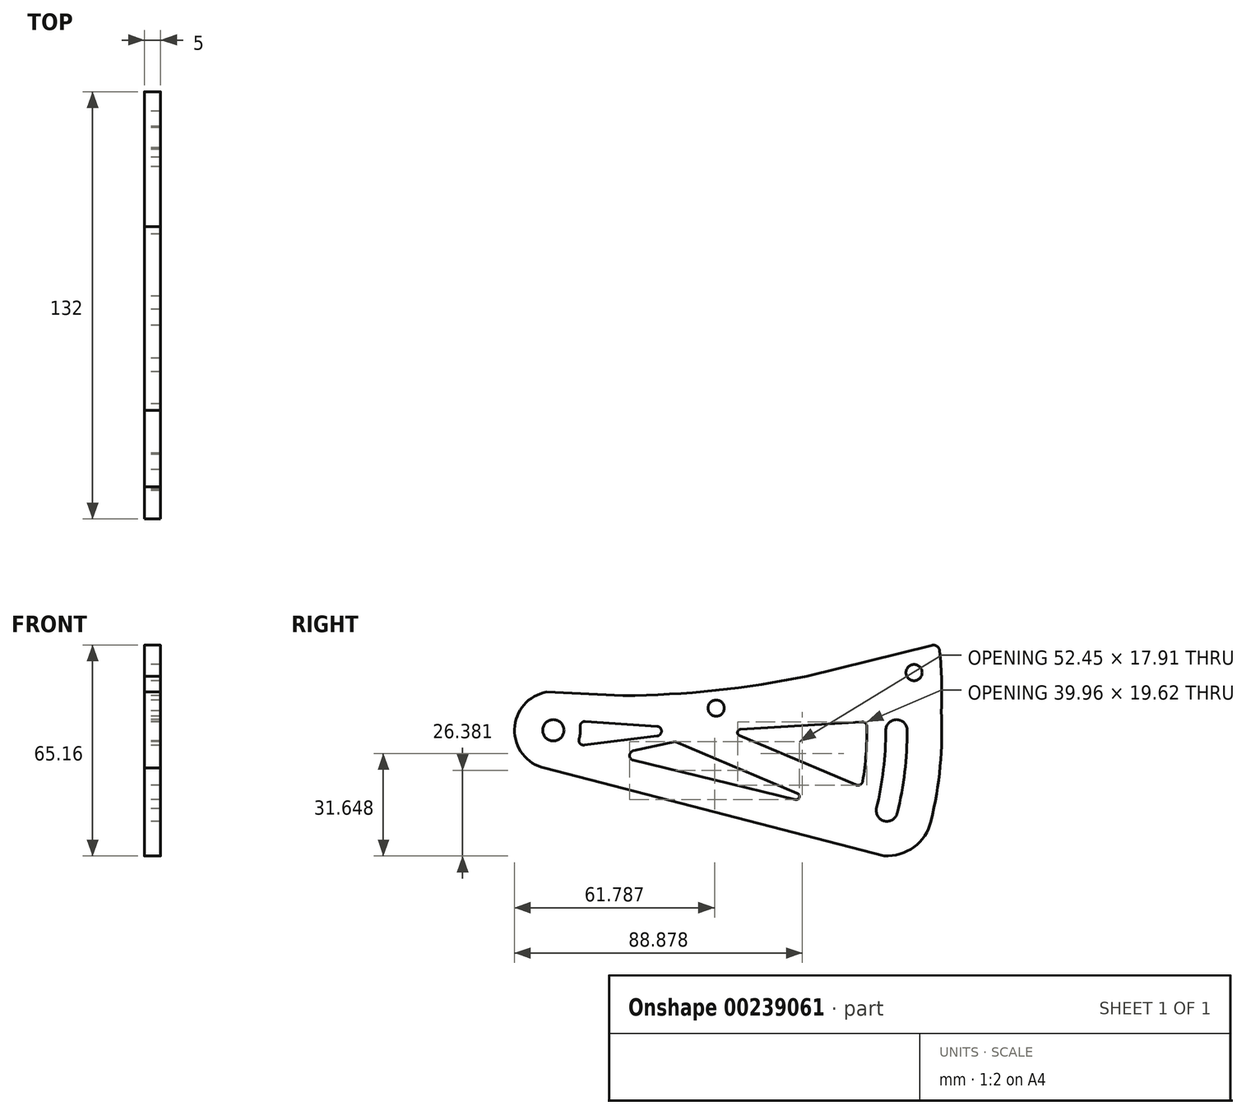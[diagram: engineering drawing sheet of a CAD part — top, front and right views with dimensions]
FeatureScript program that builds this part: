
annotation { "Feature Type Name" : "Feature", "Feature Type Description" : "" }
export const myFeature = defineFeature(function(context is Context, id is Id, definition is map)
    precondition{}
    {
        {
            var Q0;
            Q0=qCreatedBy(makeId("Right.planeOp"),FACE);
            var sketch = newSketch(context, id + "F0", { "sketchPlane" : qUnion([Q0])});
            skLineSegment(sketch, "E0", {"start": v(0, 0) * mm, "end": v(3.3, 0) * mm});
            skArc(sketch, "E1", {"start": v(98.88, -38.19) * mm, "mid": v(98.92, -38.08) * mm, "end": v(98.97, -37.97) * mm});
            skArc(sketch, "E2", {"start": v(109.3, 0) * mm, "mid": v(106, 3.3) * mm, "end": v(102.7, 0) * mm});
            skArc(sketch, "E3", {"start": v(95.75, -37.14) * mm, "mid": v(95.8, -36.99) * mm, "end": v(95.87, -36.84) * mm});
            skArc(sketch, "E4", {"start": v(106.26, -25.6) * mm, "mid": v(108.54, -12.89) * mm, "end": v(109.3, 0) * mm});
            skArc(sketch, "E5", {"start": v(116.66, -28.1) * mm, "mid": v(119.48, -11.17) * mm, "end": v(119.85, 6) * mm});
            skArc(sketch, "E6", {"start": v(99.84, -24.05) * mm, "mid": v(102.58, -28.1) * mm, "end": v(106.35, -25) * mm});
            skArc(sketch, "E7", {"start": v(0, 12) * mm, "mid": v(-11.92, 1.35) * mm, "end": v(-2.68, -11.7) * mm});
            skLineSegment(sketch, "E8", {"start": v(-3.32, -11.53) * mm, "end": v(102.18, -38.8) * mm});
            skArc(sketch, "E9.trimOffspring", {"start": v(106.35, -25) * mm, "mid": v(106.38, -25) * mm, "end": v(106.4, -25) * mm});
            skArc(sketch, "E10.trimOffspring", {"start": v(99.8, -24.22) * mm, "mid": v(101.97, -12.2) * mm, "end": v(102.7, 0) * mm});
            skArc(sketch, "E11.trimOffspring", {"start": v(99.8, -24.22) * mm, "mid": v(99.8, -24.22) * mm, "end": v(99.8, -24.22) * mm});
            skArc(sketch, "E12.trimOffspring", {"start": v(102.18, -38.8) * mm, "mid": v(111.37, -36.09) * mm, "end": v(116.66, -28.1) * mm});
            skArc(sketch, "E13", {"start": v(21.96, 10.72) * mm, "mid": v(21.96, 10.73) * mm, "end": v(21.96, 10.73) * mm});
            skArc(sketch, "E14", {"start": v(119.85, 6) * mm, "mid": v(119.96, 15.28) * mm, "end": v(119.34, 24.54) * mm});
            skArc(sketch, "E15", {"start": v(21.46, 10.73) * mm, "mid": v(22.07, 10.72) * mm, "end": v(22.67, 10.8) * mm});
            skLineSegment(sketch, "E16", {"start": v(21.83, 10.72) * mm, "end": v(-2.06, 11.82) * mm});
            skLineSegment(sketch, "E17", {"start": v(78.34, 16.72) * mm, "end": v(116.87, 26.27) * mm});
            skCircle(sketch, "E18", {"center": v(0, 0) * mm, "radius": 3.3 * mm});
            skPoint(sketch, "E19.orphan", {"position": v(21.83, 9.28) * mm});
            skPoint(sketch, "E20.third.point", {"position": v(50.09, 12.3) * mm});
            skPoint(sketch, "E20.third.point.positionSnap0", {"position": v(50.09, 13.72) * mm});
            skArc(sketch, "E21", {"start": v(21.58, 10.73) * mm, "mid": v(50.11, 12.3) * mm, "end": v(78.34, 16.72) * mm});
            skCircle(sketch, "E22", {"center": v(111.42, 17.83) * mm, "radius": 2.5 * mm});
            skCircle(sketch, "E23", {"center": v(50.3, 6.86) * mm, "radius": 2.5 * mm});
            skLineSegment(sketch, "E24", {"start": v(24.7, -9.28) * mm, "end": v(74.78, -21.38) * mm});
            skLineSegment(sketch, "E25", {"start": v(102.28, -28.03) * mm, "end": v(101.89, -27.91) * mm});
            skLineSegment(sketch, "E26", {"start": v(106, 3.3) * mm, "end": v(105.59, 3.27) * mm});
            skArc(sketch, "E27", {"start": v(7.95, -2.63) * mm, "mid": v(8.34, -0.8) * mm, "end": v(8.3, 1.08) * mm});
            skArc(sketch, "E28", {"start": v(95.57, -15.74) * mm, "mid": v(96.58, -7.32) * mm, "end": v(96.85, 1.15) * mm});
            skPoint(sketch, "E29.orphan", {"position": v(0, -3.3) * mm});
            skLineSegment(sketch, "E30.trimOffspring", {"start": v(0.97, 3.15) * mm, "end": v(0, 3.45) * mm});
            skLineSegment(sketch, "E31.trimOffspring", {"start": v(95.26, 2.63) * mm, "end": v(57.82, 0.3) * mm});
            skLineSegment(sketch, "E32", {"start": v(32.1, -1.74) * mm, "end": v(9.57, -4.58) * mm});
            skLineSegment(sketch, "E33", {"start": v(75.4, -19.5) * mm, "end": v(37.65, -3.5) * mm});
            skLineSegment(sketch, "E34", {"start": v(24.74, -6.35) * mm, "end": v(37.65, -3.5) * mm});
            skLineSegment(sketch, "E35", {"start": v(57.5, -1.62) * mm, "end": v(93.5, -16.88) * mm});
            skLineSegment(sketch, "E36.trimOffspring", {"start": v(32.02, 1.24) * mm, "end": v(9.9, 2.77) * mm});
            skLineSegment(sketch, "E37.trimOffspring", {"start": v(39.68, -4.36) * mm, "end": v(37, -3.22) * mm});
            skPoint(sketch, "E38.visualSharp", {"position": v(119.08, 26.82) * mm});
            skArc(sketch, "E38.filletArc", {"start": v(119.34, 24.54) * mm, "mid": v(118.5, 25.97) * mm, "end": v(116.87, 26.27) * mm});
            skArc(sketch, "E39.filletArc", {"start": v(9.9, 2.77) * mm, "mid": v(8.7, 2.3) * mm, "end": v(8.3, 1.08) * mm});
            skPoint(sketch, "E40.visualSharp", {"position": v(6.77, -4.94) * mm});
            skArc(sketch, "E40.filletArc", {"start": v(7.95, -2.63) * mm, "mid": v(8.22, -4.05) * mm, "end": v(9.57, -4.58) * mm});
            skArc(sketch, "E41.filletArc", {"start": v(32.1, -1.74) * mm, "mid": v(33.42, -0.21) * mm, "end": v(32.02, 1.24) * mm});
            skPoint(sketch, "E42.visualSharp", {"position": v(18.41, -7.75) * mm});
            skArc(sketch, "E42.filletArc", {"start": v(24.74, -6.35) * mm, "mid": v(23.56, -7.8) * mm, "end": v(24.7, -9.28) * mm});
            skPoint(sketch, "E43.visualSharp", {"position": v(86.65, -24.25) * mm});
            skArc(sketch, "E43.filletArc", {"start": v(74.78, -21.38) * mm, "mid": v(75.96, -20.73) * mm, "end": v(75.4, -19.5) * mm});
            skPoint(sketch, "E44.visualSharp", {"position": v(53.59, 0.03) * mm});
            skArc(sketch, "E44.filletArc", {"start": v(57.82, 0.3) * mm, "mid": v(56.9, -0.53) * mm, "end": v(57.5, -1.62) * mm});
            skArc(sketch, "E45.filletArc", {"start": v(96.85, 1.15) * mm, "mid": v(96.37, 2.23) * mm, "end": v(95.26, 2.63) * mm});
            skPoint(sketch, "E46.visualSharp", {"position": v(95.25, -17.61) * mm});
            skArc(sketch, "E46.filletArc", {"start": v(93.5, -16.88) * mm, "mid": v(94.82, -16.8) * mm, "end": v(95.57, -15.74) * mm});
            skSolve(sketch);
        }
        {
            var Q0;
            {var subQ9=sQuery(id+"F0.wireOp",EDGE,"E2");Q0=makeQuery(id+"F0.imprint","IMPRINT",FACE,{"disambiguationData":[TD([[makeQuery(id+"F0.imprint","IMPRINT",EDGE,{"derivedFrom":subQ9}),-1.0]])]});}
            var Q1;
            Q1 = qSketchRegion(id + "F0", true);
            extrude(context, id + "F1", {"entities" : qUnion([Q0, Q1]), "offsetDistance" : 25 * mm, "depth" : 5 * mm});
        }
    });
